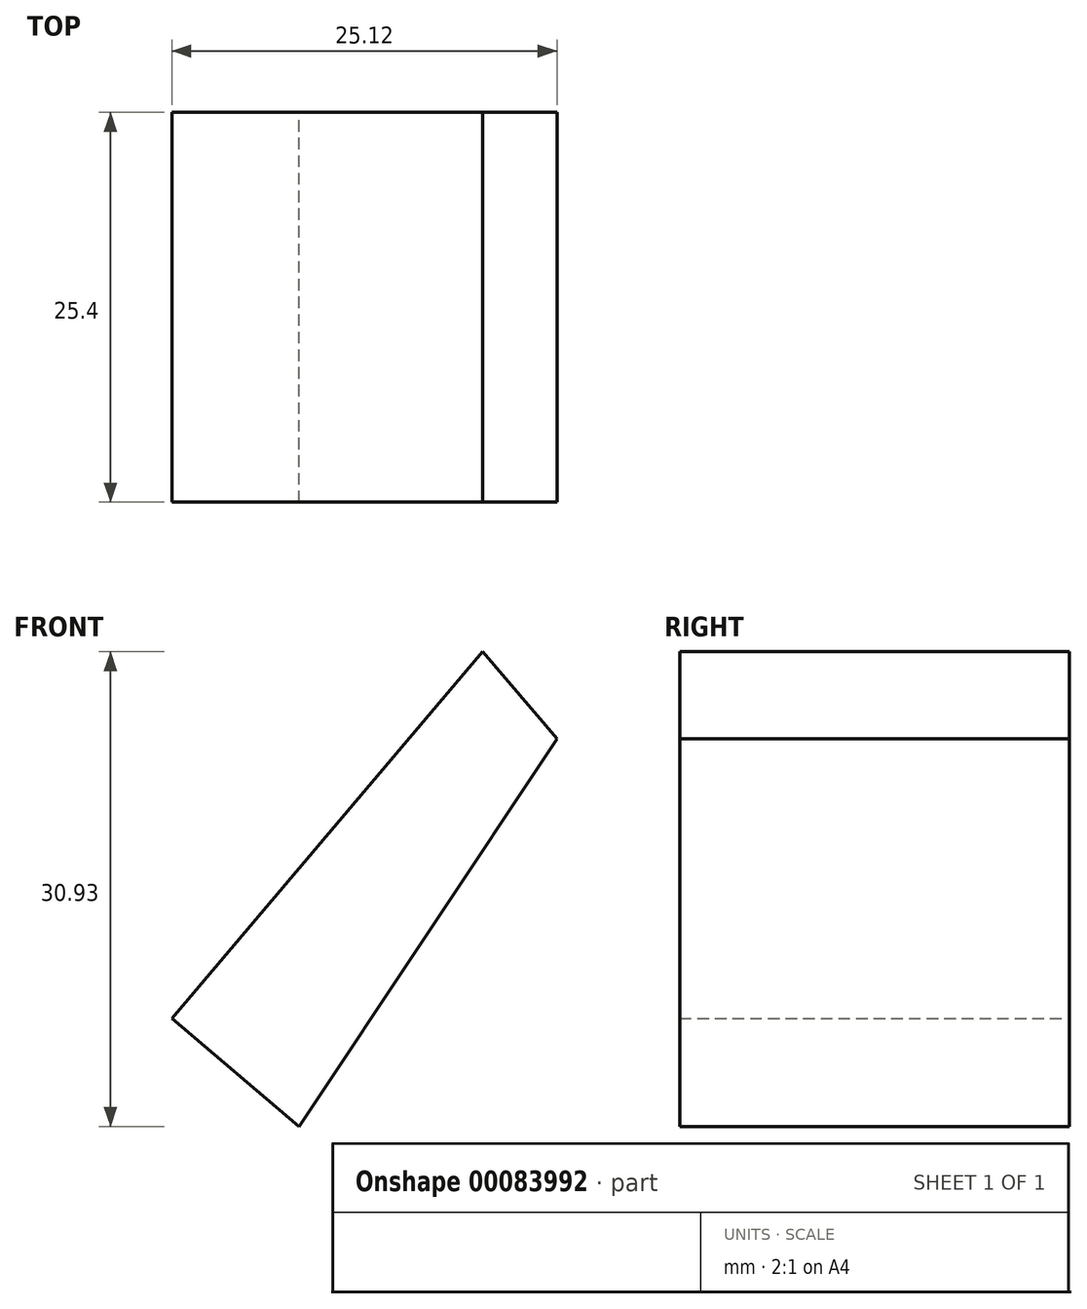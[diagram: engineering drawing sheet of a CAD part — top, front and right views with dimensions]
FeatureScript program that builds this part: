
annotation { "Feature Type Name" : "Feature", "Feature Type Description" : "" }
export const myFeature = defineFeature(function(context is Context, id is Id, definition is map)
    precondition{}
    {
        {
            var Q0;
            Q0=qCreatedBy(makeId("Front.planeOp"),FACE);
            var sketch = newSketch(context, id + "F0", { "sketchPlane" : qUnion([Q0])});
            skLineSegment(sketch, "E0", {"start": v(-50.03, 51.65) * mm, "end": v(-70.29, 27.75) * mm});
            skLineSegment(sketch, "E1", {"start": v(-70.29, 27.75) * mm, "end": v(-62, 20.72) * mm});
            skLineSegment(sketch, "E2", {"start": v(-62, 20.72) * mm, "end": v(-45.17, 45.98) * mm});
            skLineSegment(sketch, "E3", {"start": v(-45.17, 45.98) * mm, "end": v(-48.82, 20.72) * mm});
            skLineSegment(sketch, "E4", {"start": v(-48.82, 20.72) * mm, "end": v(-62, 20.72) * mm});
            skLineSegment(sketch, "E5", {"start": v(-50.03, 51.65) * mm, "end": v(-45.17, 45.98) * mm});
            skLineSegment(sketch, "E6", {"start": v(-45.17, 45.98) * mm, "end": v(-41.6, 34.49) * mm});
            skLineSegment(sketch, "E7", {"start": v(-41.6, 34.49) * mm, "end": v(-47.08, 32.78) * mm});
            skLineSegment(sketch, "E8", {"start": v(-47.08, 32.78) * mm, "end": v(-48.25, 24.64) * mm});
            skSolve(sketch);
        }
        {
            var Q0;
            Q0=makeQuery(id+"F0.imprint","IMPRINT",FACE,{"disambiguationData":[TD([[makeQuery(id+"F0.imprint","IMPRINT",EDGE,{"derivedFrom":sQuery(id+"F0.wireOp",EDGE,"E0")}),1.0]])]});
            extrude(context, id + "F1", {"entities" : qUnion([Q0]), "depth" : 25.4 * mm});
        }
    });
